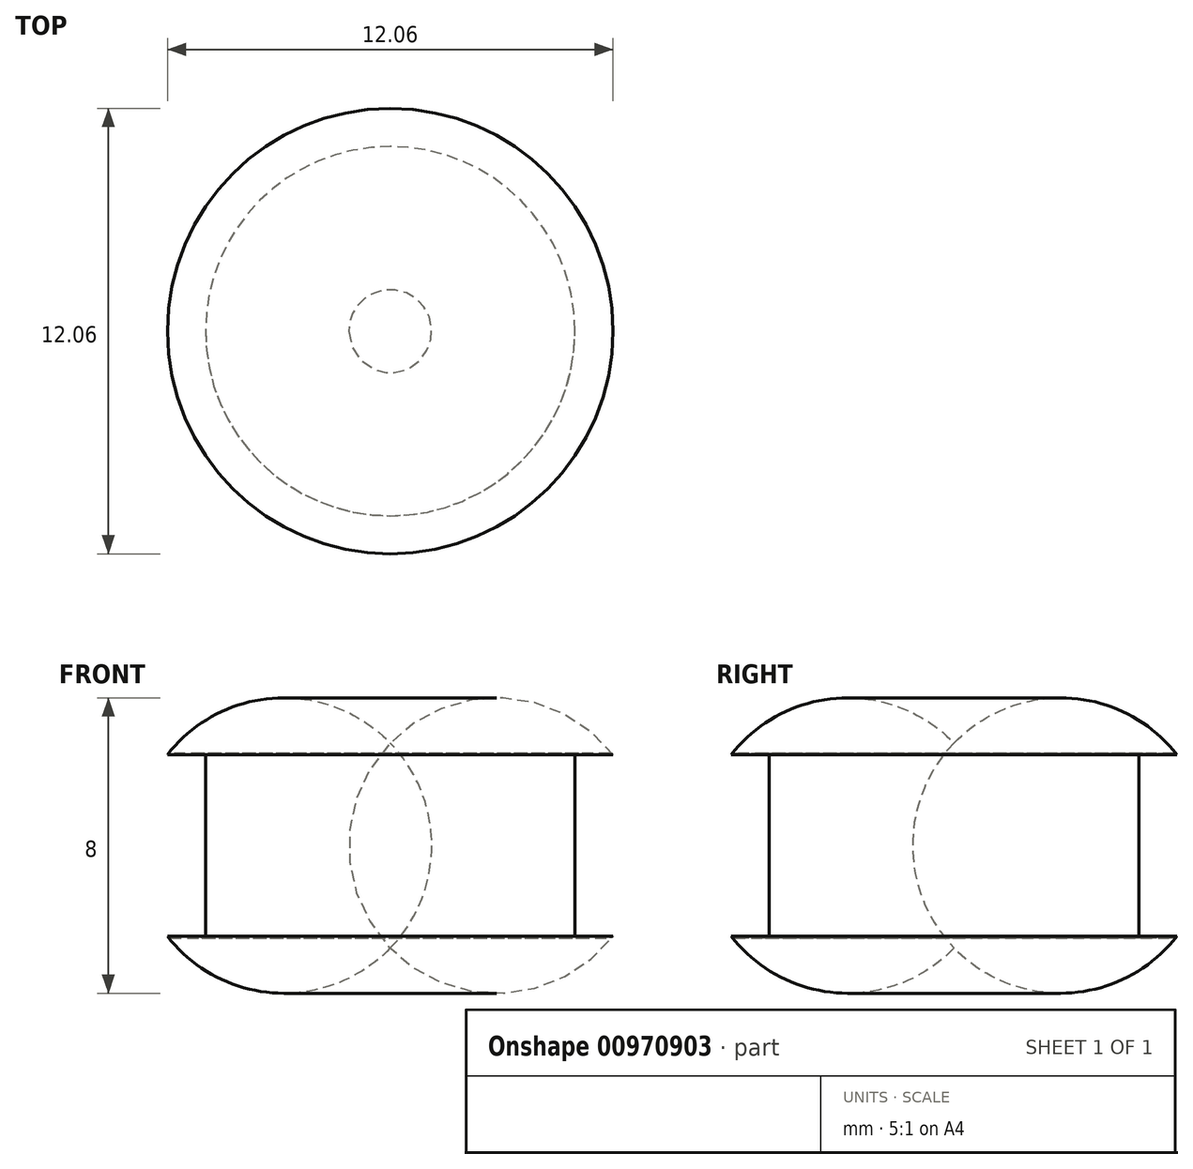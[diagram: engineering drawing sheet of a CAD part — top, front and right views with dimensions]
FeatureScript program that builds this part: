
annotation { "Feature Type Name" : "Feature", "Feature Type Description" : "" }
export const myFeature = defineFeature(function(context is Context, id is Id, definition is map)
    precondition{}
    {
        {
            var Q0;
            Q0=qCreatedBy(makeId("Top.planeOp"),FACE);
            var sketch = newSketch(context, id + "F0", { "sketchPlane" : qUnion([Q0])});
            skCircle(sketch, "E0", {"center": v(0, 0) * mm, "radius": 5 * mm});
            skSolve(sketch);
        }
        {
            var Q0;
            Q0=qCreatedBy(makeId("Front.planeOp"),FACE);
            var sketch = newSketch(context, id + "F1", { "sketchPlane" : qUnion([Q0])});
            skLineSegment(sketch, "E1", {"start": v(-5, 0) * mm, "end": v(-5, 5) * mm});
            skLineSegment(sketch, "E2", {"start": v(-5, 5) * mm, "end": v(-6, 5) * mm});
            skLineSegment(sketch, "E3", {"start": v(-5, 0) * mm, "end": v(-6, 0) * mm});
            skLineSegment(sketch, "E4.0", {"start": v(-5, 0) * mm, "end": v(5, 0) * mm, "construction": true});
            skArc(sketch, "E5", {"start": v(-6, 5) * mm, "mid": v(-6.88, 2.5) * mm, "end": v(-6, 0) * mm});
            skSolve(sketch);
        }
        {
            var Q0;
            Q0=makeQuery(id+"F1.imprint","IMPRINT",FACE,{"disambiguationData":[TD([[makeQuery(id+"F1.imprint","IMPRINT",EDGE,{"derivedFrom":sQuery(id+"F1.wireOp",EDGE,"E1")}),1.0]])]});
            var Q1;
            Q1=sQuery(id+"F0.wireOp",EDGE,"E0");
            sweep(context, id + "F2", {"profiles" : qUnion([Q0]), "path" : qUnion([Q1])});
        }
        {
            var Q0;
            Q0=makeQuery(id+"F2.opSweep","SWEPT_EDGE",EDGE,{"disambiguationData":[OSD([sQuery(id+"F0.wireOp",EDGE,"E0"),sQuery(id+"F1.wireOp",EDGE,"E2"),sQuery(id+"F1.wireOp",EDGE,"Se6l3GVB-6FFM-vzrN-t4cb-VUOn9LJQsNbt")])]});
            var Q1;
            Q1=makeQuery(id+"F2.opSweep","SWEPT_EDGE",EDGE,{"disambiguationData":[OSD([sQuery(id+"F0.wireOp",EDGE,"E0"),sQuery(id+"F1.wireOp",EDGE,"E3"),sQuery(id+"F1.wireOp",EDGE,"Se6l3GVB-6FFM-vzrN-t4cb-VUOn9LJQsNbt")])]});
            var Q2;
            Q2=makeQuery(id+"F2.opSweep","SWEPT_EDGE",EDGE,{"disambiguationData":[OSD([sQuery(id+"F0.wireOp",EDGE,"E0"),sQuery(id+"F1.wireOp",EDGE,"E1"),sQuery(id+"F1.wireOp",EDGE,"E3")])]});
            var Q3;
            Q3=makeQuery(id+"F2.opSweep","SWEPT_EDGE",EDGE,{"disambiguationData":[OSD([sQuery(id+"F0.wireOp",EDGE,"E0"),sQuery(id+"F1.wireOp",EDGE,"E1"),sQuery(id+"F1.wireOp",EDGE,"E2")])]});
            fillet(context, id + "F3", {"entities" : qUnion([Q0, Q1, Q2, Q3]), "radius" : 0.1 * mm, "tangentPropagation" : true, "allowEdgeOverflow" : false});
        }
    });
